# Revit family: ЭВАН WARMOS START 3-14 кВт
name_source: partatom
category: Оборудование
units: mm (PartAtom-declared; Revit-internal decimal feet)

## family parameters
Всегда вертикально = Да
Классификация = Нет
На основе рабочей плоскости = Да
Общий = Нет
При загрузке вырезать с полостями = Нет
Размер круглого соединителя = Использовать диаметр
Тип детали = Нормальный
Точка расчета площади = Нет

## types (8) — shared parameters
ADSK_Классификация нагрузок = Прочее
ADSK_Материал = Сталь
ADSK_Размер_Высота = 590 мм
ADSK_Размер_Длина = 200 мм
ADSK_Размер_Ширина = 118 мм
ADSK_Расход теплоносителя = 0.0 м³/ч
Dn = 25 мм
База = ЭЛЕКТРИЧЕСКИЙ ТЕПЛОГЕНЕРАТОР (КОТЕЛ)
Диапазон регулируемых температур теплоносителя, оС = От +30 до +85
Максимальная температура теплоносителя, оС = +85
Материал корпуса = Сталь
Минимальная температура теплоносителя, оС = +30
Объем колбы котла, л = 1,4
Рабочее давление, МПа = 0,07-0,3
Резьба патрубков для подключения трубопроводов теплоносителя = G1
zero-valued in all types: Отметка по умолчанию

## per-type parameters (varying)
| type | ADSK_Количество фаз | ADSK_Номинальная мощность | Потребляемая электрическая мощность при максимальной тепловой мощность  в час, кВт/ч |
| ЭВАН WARMOS START 3 кВт | 1 | 3000 Вт | 3.15 |
| ЭВАН WARMOS START 5 кВт | 1 | 5000 Вт | 5.25 |
| ЭВАН WARMOS START 7 кВт 380 В | 3 | 7000 Вт | 7.35 |
| ЭВАН WARMOS START 7 кВт 220 В | 1 | 7000 Вт | 7.35 |
| ЭВАН WARMOS START 9 кВт 380 В | 3 | 9000 Вт | 9.45 |
| ЭВАН WARMOS START 9 кВт 220 В | 1 | 9000 Вт | 9.45 |
| ЭВАН WARMOS START 12 кВт | 3 | 12000 Вт | 12.6 |
| ЭВАН WARMOS START 14 кВт | 3 | 14000 Вт | 14.7 |
